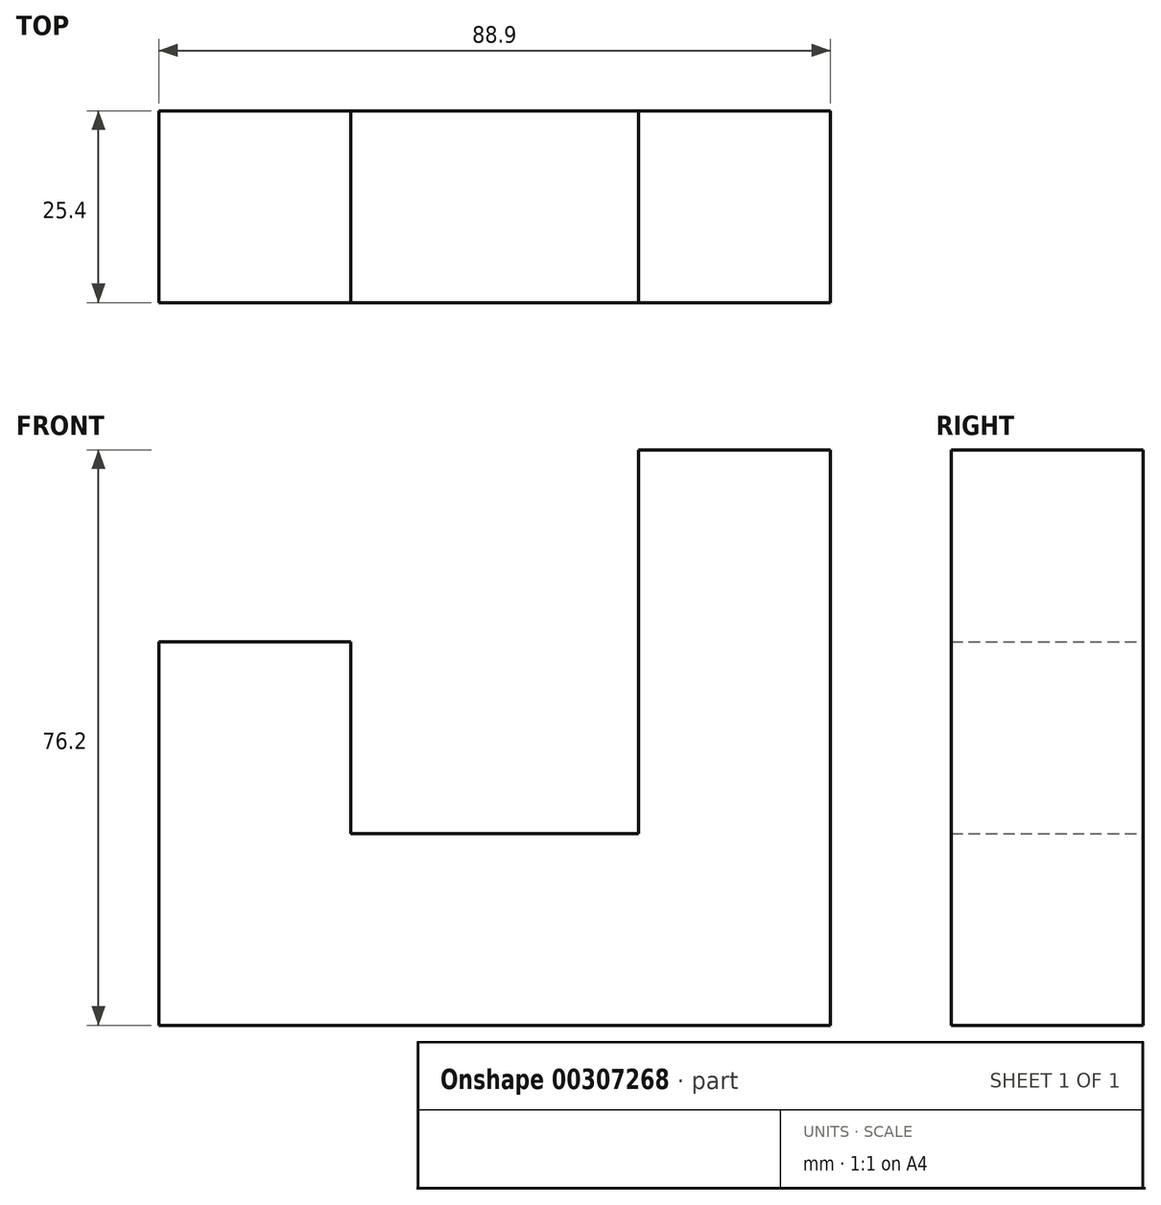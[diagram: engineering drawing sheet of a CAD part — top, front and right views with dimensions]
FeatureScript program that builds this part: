
annotation { "Feature Type Name" : "Feature", "Feature Type Description" : "" }
export const myFeature = defineFeature(function(context is Context, id is Id, definition is map)
    precondition{}
    {
        {
            var Q0;
            Q0=qCreatedBy(makeId("Front.planeOp"),FACE);
            var sketch = newSketch(context, id + "F0", { "sketchPlane" : qUnion([Q0])});
            skLineSegment(sketch, "E0", {"start": v(-77.44, -47.2) * mm, "end": v(11.46, -47.2) * mm});
            skLineSegment(sketch, "E1", {"start": v(11.46, -47.2) * mm, "end": v(11.46, 29) * mm});
            skLineSegment(sketch, "E2", {"start": v(11.46, 29) * mm, "end": v(-13.94, 29) * mm});
            skLineSegment(sketch, "E3", {"start": v(-13.94, 29) * mm, "end": v(-13.94, -21.8) * mm});
            skLineSegment(sketch, "E4", {"start": v(-13.94, -21.8) * mm, "end": v(-52.04, -21.8) * mm});
            skLineSegment(sketch, "E5", {"start": v(-52.04, -21.8) * mm, "end": v(-52.04, 3.6) * mm});
            skLineSegment(sketch, "E6", {"start": v(-52.04, 3.6) * mm, "end": v(-77.44, 3.6) * mm});
            skLineSegment(sketch, "E7", {"start": v(-77.44, 3.6) * mm, "end": v(-77.44, -47.2) * mm});
            skSolve(sketch);
        }
        {
            var Q0;
            Q0=makeQuery(id+"F0.imprint","IMPRINT",FACE,{"disambiguationData":[TD([[makeQuery(id+"F0.imprint","IMPRINT",EDGE,{"derivedFrom":sQuery(id+"F0.wireOp",EDGE,"E0")}),1.0]])]});
            extrude(context, id + "F1", {"entities" : qUnion([Q0]), "depth" : 25.4 * mm});
        }
    });
